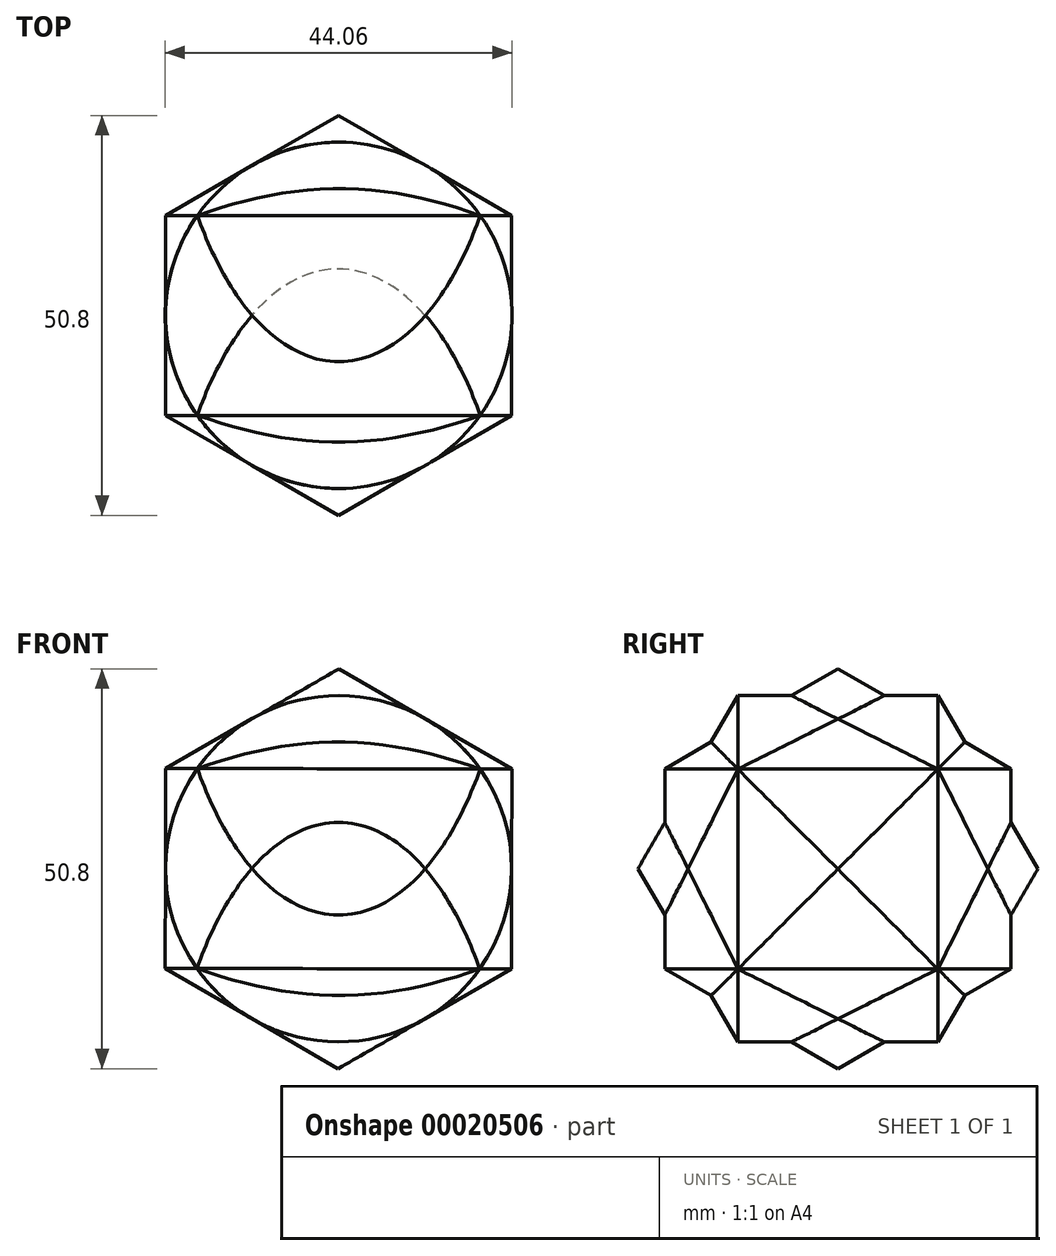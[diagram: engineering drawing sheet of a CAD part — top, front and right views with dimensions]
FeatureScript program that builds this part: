
annotation { "Feature Type Name" : "Feature", "Feature Type Description" : "" }
export const myFeature = defineFeature(function(context is Context, id is Id, definition is map)
    precondition{}
    {
        {
            var Q0;
            Q0=qCreatedBy(makeId("Front.planeOp"),FACE);
            var sketch = newSketch(context, id + "F0", { "sketchPlane" : qUnion([Q0])});
            skCircle(sketch, "E0.cCircle", {"center": v(0, 0) * mm, "radius": 22 * mm, "construction": true});
            skLineSegment(sketch, "E0.0", {"start": v(-21.97, 12.75) * mm, "end": v(0.06, 25.4) * mm});
            skLineSegment(sketch, "E0.1", {"start": v(0.06, 25.4) * mm, "end": v(22.03, 12.65) * mm});
            skLineSegment(sketch, "E0.2", {"start": v(22.03, 12.65) * mm, "end": v(21.97, -12.75) * mm});
            skLineSegment(sketch, "E0.3", {"start": v(21.97, -12.75) * mm, "end": v(-0.06, -25.4) * mm});
            skLineSegment(sketch, "E0.4", {"start": v(-0.06, -25.4) * mm, "end": v(-22.03, -12.65) * mm});
            skLineSegment(sketch, "E0.5", {"start": v(-22.03, -12.65) * mm, "end": v(-21.97, 12.75) * mm});
            skPoint(sketch, "E0.0.midPoint", {"position": v(-10.95, 19.08) * mm});
            skLineSegment(sketch, "E1", {"start": v(0.06, 25.4) * mm, "end": v(-0.06, -25.4) * mm});
            skSolve(sketch);
        }
        {
            var Q0;
            Q0=makeQuery(id+"F0.imprint","IMPRINT",FACE,{"disambiguationData":[TD([[makeQuery(id+"F0.imprint","IMPRINT",EDGE,{"derivedFrom":sQuery(id+"F0.wireOp",EDGE,"E0.0")}),-1.0]])]});
            var Q1;
            Q1=sQuery(id+"F0.wireOp",EDGE,"E1");
            revolve(context, id + "F1", {"entities" : qUnion([Q0]), "axis" : qUnion([Q1]), "revolveType" : RevolveType.FULL});
        }
        {
            var Q0;
            Q0=qCreatedBy(makeId("Top.planeOp"),FACE);
            var sketch = newSketch(context, id + "F2", { "sketchPlane" : qUnion([Q0])});
            skCircle(sketch, "E2.cCircle", {"center": v(0, 0) * mm, "radius": 22 * mm, "construction": true});
            skLineSegment(sketch, "E2.0", {"start": v(-22, 12.7) * mm, "end": v(0, 25.4) * mm});
            skLineSegment(sketch, "E2.1", {"start": v(0, 25.4) * mm, "end": v(22, 12.7) * mm});
            skLineSegment(sketch, "E2.2", {"start": v(22, 12.7) * mm, "end": v(22, -12.7) * mm});
            skLineSegment(sketch, "E2.3", {"start": v(22, -12.7) * mm, "end": v(0, -25.4) * mm});
            skLineSegment(sketch, "E2.4", {"start": v(0, -25.4) * mm, "end": v(-22, -12.7) * mm});
            skLineSegment(sketch, "E2.5", {"start": v(-22, -12.7) * mm, "end": v(-22, 12.7) * mm});
            skPoint(sketch, "E2.0.midPoint", {"position": v(-11, 19.05) * mm});
            skLineSegment(sketch, "E3", {"start": v(0, 25.4) * mm, "end": v(0, -25.4) * mm});
            skSolve(sketch);
        }
        {
            var Q0;
            Q0=makeQuery(id+"F2.imprint","IMPRINT",FACE,{"disambiguationData":[TD([[makeQuery(id+"F2.imprint","IMPRINT",EDGE,{"derivedFrom":sQuery(id+"F2.wireOp",EDGE,"E2.0")}),-1.0]])]});
            var Q1;
            Q1=sQuery(id+"F2.wireOp",EDGE,"E3");
            revolve(context, id + "F3", {"operationType" : NewBodyOperationType.ADD, "entities" : qUnion([Q0]), "axis" : qUnion([Q1]), "revolveType" : RevolveType.FULL});
        }
    });
